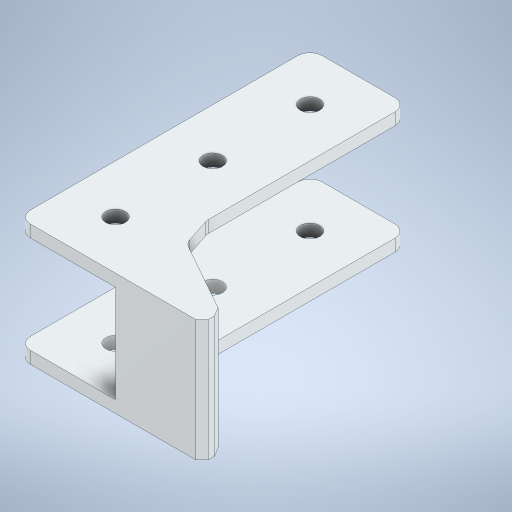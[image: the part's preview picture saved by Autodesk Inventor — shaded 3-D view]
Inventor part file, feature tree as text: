
AUTODESK INVENTOR PART (.ipt)
format: ipt  version: 2024 (Build 280153000, 153)  size: 431,104 bytes
history: native  units: in
note: dims shown in document units (in); Inventor stores cm internally (conversion verified against a paired STEP export)
features: sketch x13, extrude x12, projected_geometry x9, chamfer x5, fillet x2
ambient origin geometry x8: Origin, YZ Plane, XZ Plane, XY Plane, X Axis, Y Axis, Z Axis, Center Point
bodies: Solid1 (feature_tree)
feature tree (41):
  extrude  "Extrusion1"  Depth=0.125in
  extrude  "Extrusion2"  Depth=0.6875in TaperAngle=0.0deg
  extrude  "Extrusion3"  Depth=2.875in TaperAngle=0.0deg
  extrude  "Extrusion4"  Depth=1.0in TaperAngle=0.0deg
  extrude  "Extrusion5"  Depth=0.125in TaperAngle=45.0deg
  extrude  "Extrusion6"  Depth=0.125in TaperAngle=45.0deg
  extrude  "Extrusion7"  Depth=0.125in TaperAngle=45.0deg
  extrude  "Extrusion8"  Depth=1.0in TaperAngle=0.0deg
  chamfer  "Chamfer1"  Distance=1.0in
  extrude  "Extrusion9"  Depth=0.125in TaperAngle=45.0deg
  chamfer  "Chamfer2"  [1 undecoded]
  extrude  "Extrusion10"  [1 undecoded]
  chamfer  "Chamfer3"  [1 undecoded]
  chamfer  "Chamfer4"  [1 undecoded]
  extrude  "Extrusion11"  [1 undecoded]
  sketch  "Sketch12"
  extrude  "Extrusion12"  [1 undecoded]
  fillet  "Fillet2"  [1 undecoded]
  chamfer  "Chamfer5"  [1 undecoded]
  sketch  "Sketch1"  dims[d0=1.125in d1=0.0in d2=0.125in]
  projected_geometry  "Projected Loop1"
  sketch  "Sketch2"  dims[d3=5.75in d4=0.0in d5=0.6875in d6=0.0in]
  projected_geometry  "Projected Loop2"
  sketch  "Sketch3"  dims[d7=2.875in d8=0.0in d9=2.875in d10=0.0in]
  sketch  "Sketch4"  dims[d11=1.0in d12=0.0in d13=1.875in d14=0.0in]
  projected_geometry  "Projected Loop3"
  sketch  "Sketch5"  dims[d15=3.0625in d16=0.0in d17=0.125in d18=0.125in d19=45.0deg]
  projected_geometry  "Projected Loop4"
  projected_geometry  "Projected Loop5"
  sketch  "Sketch6"  dims[d20=3.0625in d21=0.0in d22=0.25in d23=0.125in d24=45.0deg]
  projected_geometry  "Projected Loop6"
  sketch  "Sketch7"  dims[d25=5.125in d26=0.0in d27=0.0625in d28=0.125in d29=45.0deg]
  projected_geometry  "Projected Loop7"
  sketch  "Sketch8"  dims[d30=0.1875in d31=0.125in d32=45.0deg d33=20.9375in d34=0.0in d35=1.0in d36=0.0in]
  projected_geometry  "Projected Loop8"
  sketch  "Sketch9"  dims[d37=0.125in d38=0.0625in d39=0.125in d40=45.0deg]
  projected_geometry  "Projected Loop9"
  sketch  "Sketch10"
  sketch  "Sketch11"
  sketch  "Sketch13"
  fillet  "Fillet1"  [1 undecoded]
note: 9 required parameter values undecoded (feature->parameter linkage not recoverable at this tier; creation-order binding heuristic only, values carry confidence <= 0.55)
